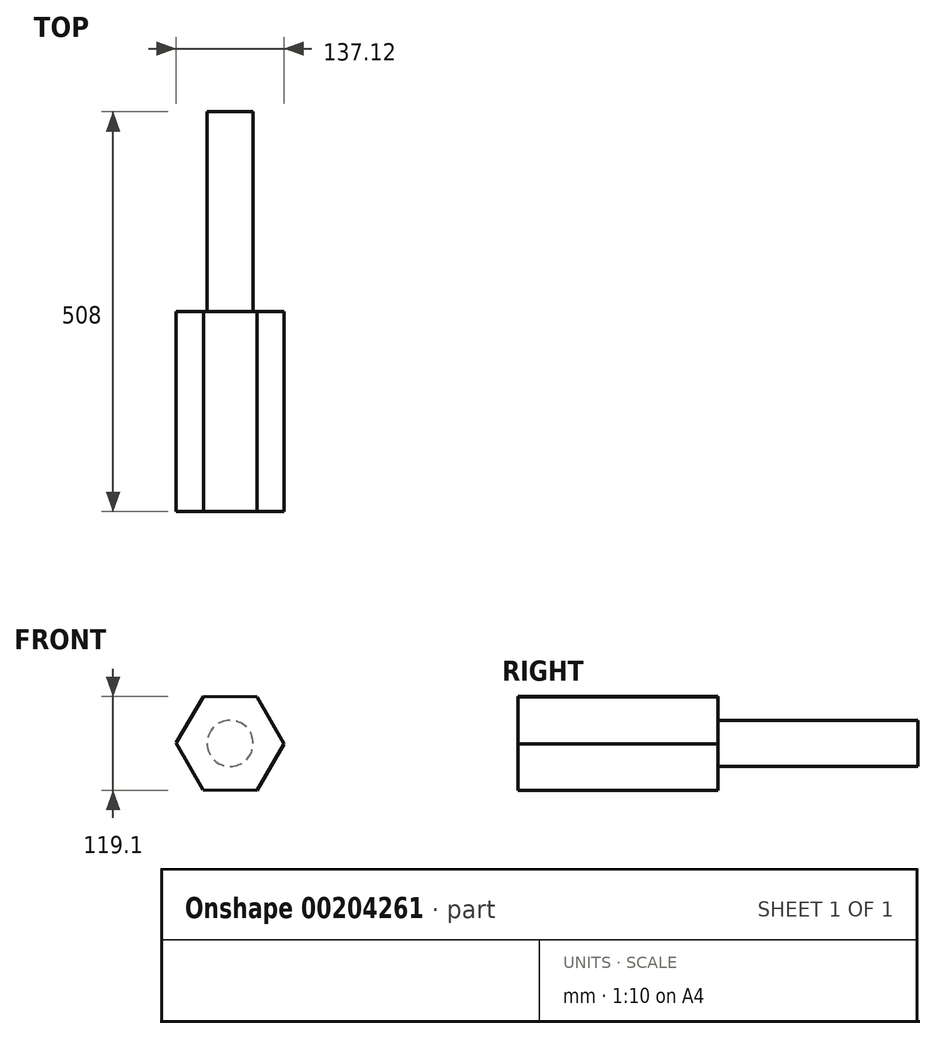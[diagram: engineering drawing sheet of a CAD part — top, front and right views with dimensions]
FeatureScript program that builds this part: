
annotation { "Feature Type Name" : "Feature", "Feature Type Description" : "" }
export const myFeature = defineFeature(function(context is Context, id is Id, definition is map)
    precondition{}
    {
        {
            var Q0;
            Q0=qCreatedBy(makeId("Front.planeOp"),FACE);
            var sketch = newSketch(context, id + "F0", { "sketchPlane" : qUnion([Q0])});
            skCircle(sketch, "E0.cCircle", {"center": v(0, 0) * mm, "radius": 59.37 * mm, "construction": true});
            skLineSegment(sketch, "E0.0", {"start": v(68.56, -0.36) * mm, "end": v(33.97, -59.55) * mm});
            skLineSegment(sketch, "E0.1", {"start": v(33.97, -59.55) * mm, "end": v(-34.59, -59.2) * mm});
            skLineSegment(sketch, "E0.2", {"start": v(-34.59, -59.2) * mm, "end": v(-68.56, 0.36) * mm});
            skLineSegment(sketch, "E0.3", {"start": v(-68.56, 0.36) * mm, "end": v(-33.97, 59.55) * mm});
            skLineSegment(sketch, "E0.4", {"start": v(-33.97, 59.55) * mm, "end": v(34.59, 59.2) * mm});
            skLineSegment(sketch, "E0.5", {"start": v(34.59, 59.2) * mm, "end": v(68.56, -0.36) * mm});
            skPoint(sketch, "E0.0.midPoint", {"position": v(51.26, -29.96) * mm});
            skSolve(sketch);
        }
        {
            var Q0;
            Q0=makeQuery(id+"F0.imprint","IMPRINT",FACE,{"disambiguationData":[TD([[makeQuery(id+"F0.imprint","IMPRINT",EDGE,{"derivedFrom":sQuery(id+"F0.wireOp",EDGE,"E0.0")}),-1.0]])]});
            extrude(context, id + "F1", {"entities" : qUnion([Q0]), "depth" : 254 * mm});
        }
        {
            var Q0;
            Q0=makeQuery(id+"F1.opExtrude","CAP_FACE",FACE,{"disambiguationData":[OSD([sQuery(id+"F0.wireOp",EDGE,"E0.0"),sQuery(id+"F0.wireOp",EDGE,"E0.1"),sQuery(id+"F0.wireOp",EDGE,"E0.2"),sQuery(id+"F0.wireOp",EDGE,"E0.3"),sQuery(id+"F0.wireOp",EDGE,"E0.4"),sQuery(id+"F0.wireOp",EDGE,"E0.5")])],"isStart":false});
            var sketch = newSketch(context, id + "F2", { "sketchPlane" : qUnion([Q0])});
            skCircle(sketch, "E1", {"center": v(0, 0) * mm, "radius": 29.2 * mm});
            skSolve(sketch);
        }
        {
            var Q0;
            Q0=sQuery(id+"F2.wireOp",EDGE,"E1");
            extrude(context, id + "F3", {"bodyType" : ToolBodyType.SURFACE, "surfaceEntities" : qUnion([Q0]), "depth" : 254 * mm});
        }
        {
            var Q0;
            Q0=makeQuery(id+"F1.opExtrude","CAP_FACE",FACE,{"disambiguationData":[OSD([sQuery(id+"F0.wireOp",EDGE,"E0.0"),sQuery(id+"F0.wireOp",EDGE,"E0.1"),sQuery(id+"F0.wireOp",EDGE,"E0.2"),sQuery(id+"F0.wireOp",EDGE,"E0.3"),sQuery(id+"F0.wireOp",EDGE,"E0.4"),sQuery(id+"F0.wireOp",EDGE,"E0.5")])],"isStart":true});
            var sketch = newSketch(context, id + "F4", { "sketchPlane" : qUnion([Q0])});
            skCircle(sketch, "E2", {"center": v(0, 0) * mm, "radius": 29.28 * mm});
            skSolve(sketch);
        }
        {
            var Q0;
            Q0 = qSketchRegion(id + "F4", true);
            extrude(context, id + "F5", {"entities" : qUnion([Q0]), "operationType" : NewBodyOperationType.ADD, "depth" : 254 * mm});
        }
    });
